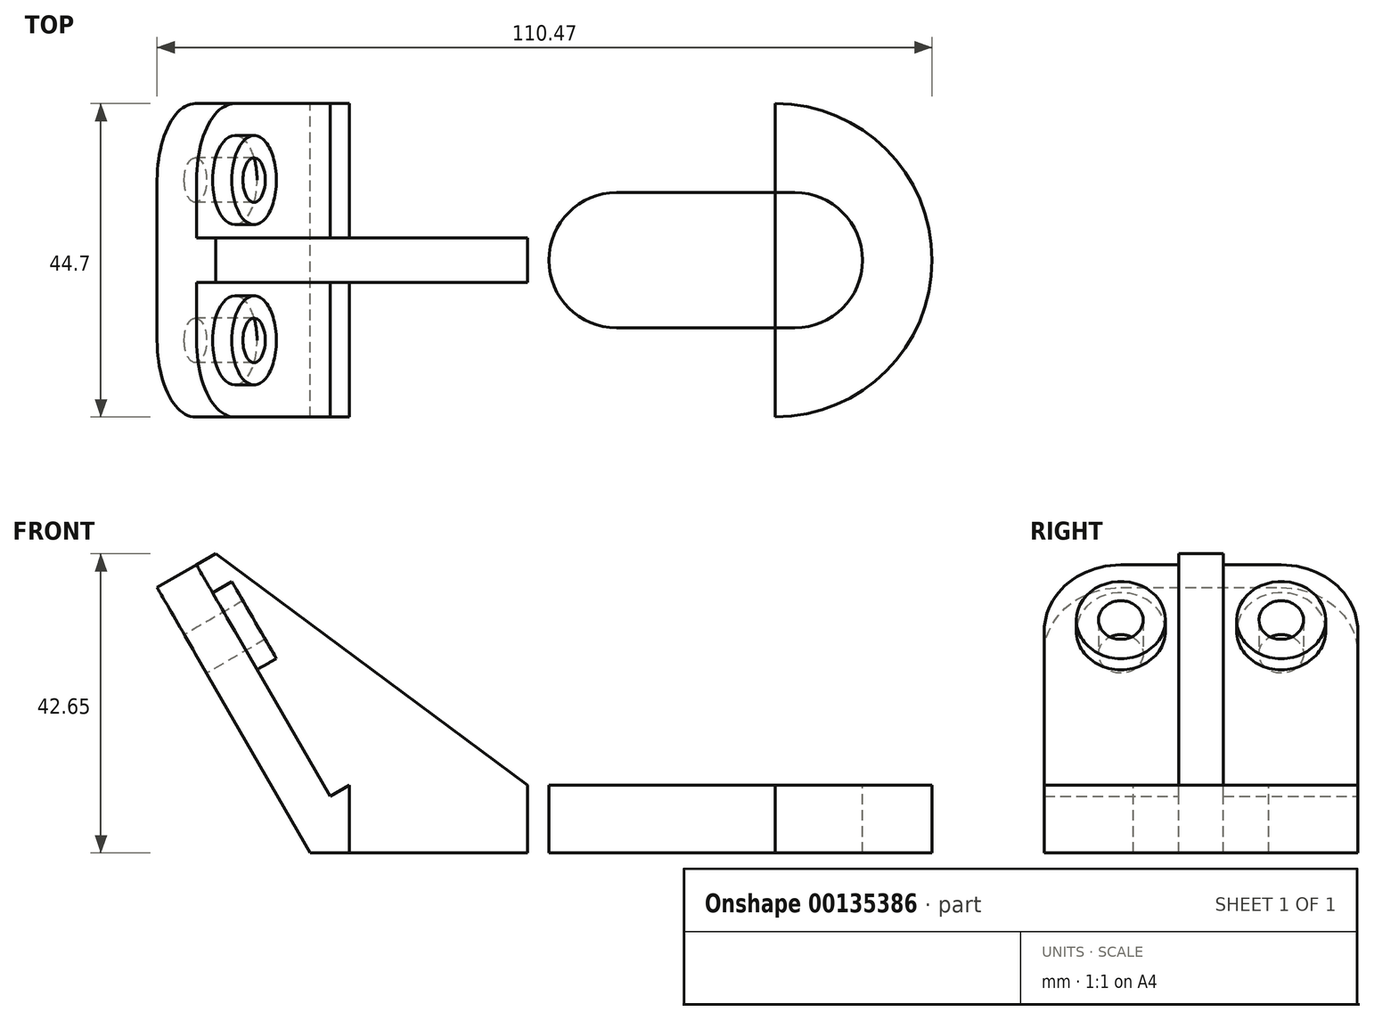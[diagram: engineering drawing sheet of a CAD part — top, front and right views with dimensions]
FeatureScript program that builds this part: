
annotation { "Feature Type Name" : "Feature", "Feature Type Description" : "" }
export const myFeature = defineFeature(function(context is Context, id is Id, definition is map)
    precondition{}
    {
        {
            var Q0;
            Q0=qCreatedBy(makeId("Front.planeOp"),FACE);
            var sketch = newSketch(context, id + "F0", { "sketchPlane" : qUnion([Q0])});
            skLineSegment(sketch, "E0", {"start": v(63.5, 0) * mm, "end": v(0, 0) * mm, "construction": true});
            skLineSegment(sketch, "E1", {"start": v(0, 0) * mm, "end": v(-19.05, 33) * mm, "construction": true});
            skLineSegment(sketch, "E2.0", {"start": v(2.79, 4.83) * mm, "end": v(-16.26, 37.82) * mm});
            skLineSegment(sketch, "E2.1", {"start": v(63.5, 4.83) * mm, "end": v(2.79, 4.83) * mm});
            skLineSegment(sketch, "E3.0", {"start": v(-2.79, -4.83) * mm, "end": v(-24.62, 33) * mm});
            skLineSegment(sketch, "E3.1", {"start": v(63.5, -4.83) * mm, "end": v(-2.79, -4.83) * mm});
            skLineSegment(sketch, "E4", {"start": v(-24.62, 33) * mm, "end": v(-16.26, 37.82) * mm});
            skLineSegment(sketch, "E5", {"start": v(63.5, 4.83) * mm, "end": v(63.5, -4.83) * mm});
            skLineSegment(sketch, "E6", {"start": v(-16.26, 37.82) * mm, "end": v(28.19, 4.83) * mm});
            skSolve(sketch);
        }
        {
            var Q0;
            {var subQ1=sQuery(id+"F0.wireOp",EDGE,"E2.0");Q0=makeQuery(id+"F0.imprint","IMPRINT",FACE,{"disambiguationData":[TD([[makeQuery(id+"F0.imprint","IMPRINT",EDGE,{"derivedFrom":subQ1}),1.0]])]});}
            extrude(context, id + "F1", {"entities" : qUnion([Q0]), "endBound" : BoundingType.SYMMETRIC, "depth" : 44.7 * mm});
        }
        {
            var Q0;
            {var subQ0=sQuery(id+"F0.wireOp",EDGE,"E2.0");Q0=makeQuery(id+"F0.imprint","IMPRINT",FACE,{"disambiguationData":[TD([[makeQuery(id+"F0.imprint","IMPRINT",EDGE,{"derivedFrom":subQ0}),-1.0]])]});}
            extrude(context, id + "F2", {"entities" : qUnion([Q0]), "operationType" : NewBodyOperationType.ADD, "endBound" : BoundingType.SYMMETRIC, "depth" : 6.35 * mm});
        }
        {
            var Q0;
            Q0=makeQuery(id+"F1.opExtrude","CAP_EDGE",EDGE,{"disambiguationData":[OSD([sQuery(id+"F0.wireOp",EDGE,"E4")])],"isStart":false});
            var Q1;
            Q1=makeQuery(id+"F1.opExtrude","CAP_EDGE",EDGE,{"disambiguationData":[OSD([sQuery(id+"F0.wireOp",EDGE,"E4")])],"isStart":true});
            fillet(context, id + "F3", {"entities" : qUnion([Q0, Q1]), "radius" : 10.92 * mm, "tangentPropagation" : true, "allowEdgeOverflow" : false});
        }
        {
            var Q0;
            Q0=makeQuery(id+"F1.opExtrude","SWEPT_FACE",FACE,{"disambiguationData":[OSD([sQuery(id+"F0.wireOp",EDGE,"E2.1")])]});
            var sketch = newSketch(context, id + "F4", { "sketchPlane" : qUnion([Q0])});
            skLineSegment(sketch, "E7", {"start": v(40.89, 0) * mm, "end": v(66.29, 0) * mm, "construction": true});
            skPoint(sketch, "E7.startSnap0", {"position": v(28.19, 0) * mm});
            skPoint(sketch, "E7.endSnap0", {"position": v(28.19, 0) * mm});
            skArc(sketch, "E8", {"start": v(63.5, -22.35) * mm, "mid": v(85.85, 0) * mm, "end": v(63.5, 22.35) * mm});
            skArc(sketch, "E9.0.startCap", {"start": v(40.89, -9.65) * mm, "mid": v(31.23, 0) * mm, "end": v(40.89, 9.65) * mm});
            skArc(sketch, "E9.0.endCap", {"start": v(66.29, 9.65) * mm, "mid": v(75.94, 0) * mm, "end": v(66.29, -9.65) * mm});
            skLineSegment(sketch, "E9.0.left", {"start": v(40.89, 9.65) * mm, "end": v(66.29, 9.65) * mm});
            skLineSegment(sketch, "E9.0.right", {"start": v(40.89, -9.65) * mm, "end": v(66.29, -9.65) * mm});
            skSolve(sketch);
        }
        {
            var Q0;
            {var subQ0=sQuery(id+"F4.wireOp",EDGE,"E8");Q0=makeQuery(id+"F4.imprint","IMPRINT",FACE,{"disambiguationData":[TD([[makeQuery(id+"F4.imprint","IMPRINT",EDGE,{"derivedFrom":subQ0}),1.0]])]});}
            extrude(context, id + "F5", {"entities" : qUnion([Q0]), "operationType" : NewBodyOperationType.ADD, "oppositeDirection" : true, "depth" : 9.65 * mm});
        }
        {
            var Q0;
            {var subQ0=sQuery(id+"F4.wireOp",EDGE,"E9.0.startCap");Q0=makeQuery(id+"F4.imprint","IMPRINT",FACE,{"disambiguationData":[TD([[makeQuery(id+"F4.imprint","IMPRINT",EDGE,{"derivedFrom":subQ0}),-1.0]])]});}
            extrude(context, id + "F6", {"entities" : qUnion([Q0]), "operationType" : NewBodyOperationType.REMOVE, "oppositeDirection" : true, "depth" : 25.4 * mm});
        }
        {
            var Q0;
            Q0=makeQuery(id+"F1.opExtrude","SWEPT_FACE",FACE,{"disambiguationData":[OSD([sQuery(id+"F0.wireOp",EDGE,"E3.0")])]});
            var sketch = newSketch(context, id + "F7", { "sketchPlane" : qUnion([Q0])});
            skLineSegment(sketch, "E10.0", {"start": v(-22.35, -2.79) * mm, "end": v(-22.35, 29.96) * mm});
            skLineSegment(sketch, "E11", {"start": v(-22.35, 29.96) * mm, "end": v(-11.43, 29.96) * mm});
            skLineSegment(sketch, "E12.0", {"start": v(22.35, -2.79) * mm, "end": v(22.35, 29.96) * mm});
            skLineSegment(sketch, "E13", {"start": v(22.35, 29.96) * mm, "end": v(11.43, 29.96) * mm});
            skCircle(sketch, "E14", {"center": v(-11.43, 29.96) * mm, "radius": 6.35 * mm});
            skCircle(sketch, "E15", {"center": v(-11.43, 29.96) * mm, "radius": 3.18 * mm});
            skCircle(sketch, "E16", {"center": v(11.43, 29.96) * mm, "radius": 6.35 * mm});
            skCircle(sketch, "E17", {"center": v(11.43, 29.96) * mm, "radius": 3.18 * mm});
            skSolve(sketch);
        }
        {
            var Q0;
            {var subQ0=sQuery(id+"F0.wireOp",EDGE,"E6");var subQ1=sQuery(id+"F0.wireOp",EDGE,"E2.1");var subQ2=sQuery(id+"F0.wireOp",EDGE,"E2.0");Q0=makeQuery(id+"F2.boolean.opBoolean","SPLIT",FACE,{"disambiguationData":[TD([makeQuery(id+"F2.opExtrude","CAP_FACE",FACE,{"disambiguationData":[OSD([subQ2,subQ1,subQ0])],"isStart":true})])],"derivedFrom":makeQuery(id+"F1.opExtrude","SWEPT_FACE",FACE,{"disambiguationData":[OSD([subQ2])]})});}
            var sketch = newSketch(context, id + "F8", { "sketchPlane" : qUnion([Q0])});
            skLineSegment(sketch, "E18.0.0", {"start": v(-3.18, 40.89) * mm, "end": v(-11.43, 40.89) * mm});
            skArc(sketch, "E18.0.1", {"start": v(-11.43, 40.89) * mm, "mid": v(-19.15, 37.69) * mm, "end": v(-22.35, 29.96) * mm});
            skLineSegment(sketch, "E18.0.2", {"start": v(-22.35, 29.96) * mm, "end": v(-22.35, 2.79) * mm});
            skLineSegment(sketch, "E18.0.3", {"start": v(-22.35, 2.79) * mm, "end": v(-3.18, 2.79) * mm});
            skLineSegment(sketch, "E18.0.4", {"start": v(-3.18, 2.79) * mm, "end": v(-3.18, 40.89) * mm});
            skCircle(sketch, "E19.0", {"center": v(-11.43, 29.96) * mm, "radius": 6.35 * mm});
            skCircle(sketch, "E20.0", {"center": v(11.43, 29.96) * mm, "radius": 6.35 * mm});
            skSolve(sketch);
        }
        {
            var Q0;
            Q0=makeQuery(id+"F7.imprint","IMPRINT",FACE,{"disambiguationData":[TD([[makeQuery(id+"F7.imprint","IMPRINT",EDGE,{"derivedFrom":sQuery(id+"F7.wireOp",EDGE,"E17")}),1.0]])]});
            var Q1;
            Q1=makeQuery(id+"F7.imprint","IMPRINT",FACE,{"disambiguationData":[TD([[makeQuery(id+"F7.imprint","IMPRINT",EDGE,{"derivedFrom":sQuery(id+"F7.wireOp",EDGE,"E15")}),1.0]])]});
            var Q2;
            {var subQ0=sQuery(id+"F0.wireOp",EDGE,"E6");var subQ1=sQuery(id+"F0.wireOp",EDGE,"E2.1");var subQ2=sQuery(id+"F0.wireOp",EDGE,"E2.0");Q2=makeQuery(id+"F2.boolean.opBoolean","SPLIT",FACE,{"disambiguationData":[TD([makeQuery(id+"F2.opExtrude","CAP_FACE",FACE,{"disambiguationData":[OSD([subQ2,subQ1,subQ0])],"isStart":false})])],"derivedFrom":makeQuery(id+"F1.opExtrude","SWEPT_FACE",FACE,{"disambiguationData":[OSD([subQ2])]})});}
            extrude(context, id + "F9", {"entities" : qUnion([Q0, Q1]), "operationType" : NewBodyOperationType.REMOVE, "endBound" : BoundingType.UP_TO_SURFACE, "oppositeDirection" : true, "endBoundEntityFace" : qUnion([Q2]), "depth" : 25.4 * mm});
        }
        {
            var Q0;
            Q0=makeQuery(id+"F8.imprint","IMPRINT",FACE,{"disambiguationData":[TD([[makeQuery(id+"F8.imprint","IMPRINT",EDGE,{"derivedFrom":sQuery(id+"F8.wireOp",EDGE,"E19.0")}),-1.0]])]});
            var Q1;
            Q1=makeQuery(id+"F8.imprint","IMPRINT",FACE,{"disambiguationData":[TD([[makeQuery(id+"F8.imprint","IMPRINT",EDGE,{"derivedFrom":sQuery(id+"F8.wireOp",EDGE,"E20.0")}),-1.0]])]});
            extrude(context, id + "F10", {"entities" : qUnion([Q0, Q1]), "operationType" : NewBodyOperationType.REMOVE, "oppositeDirection" : true, "depth" : 3.17 * mm});
        }
    });
